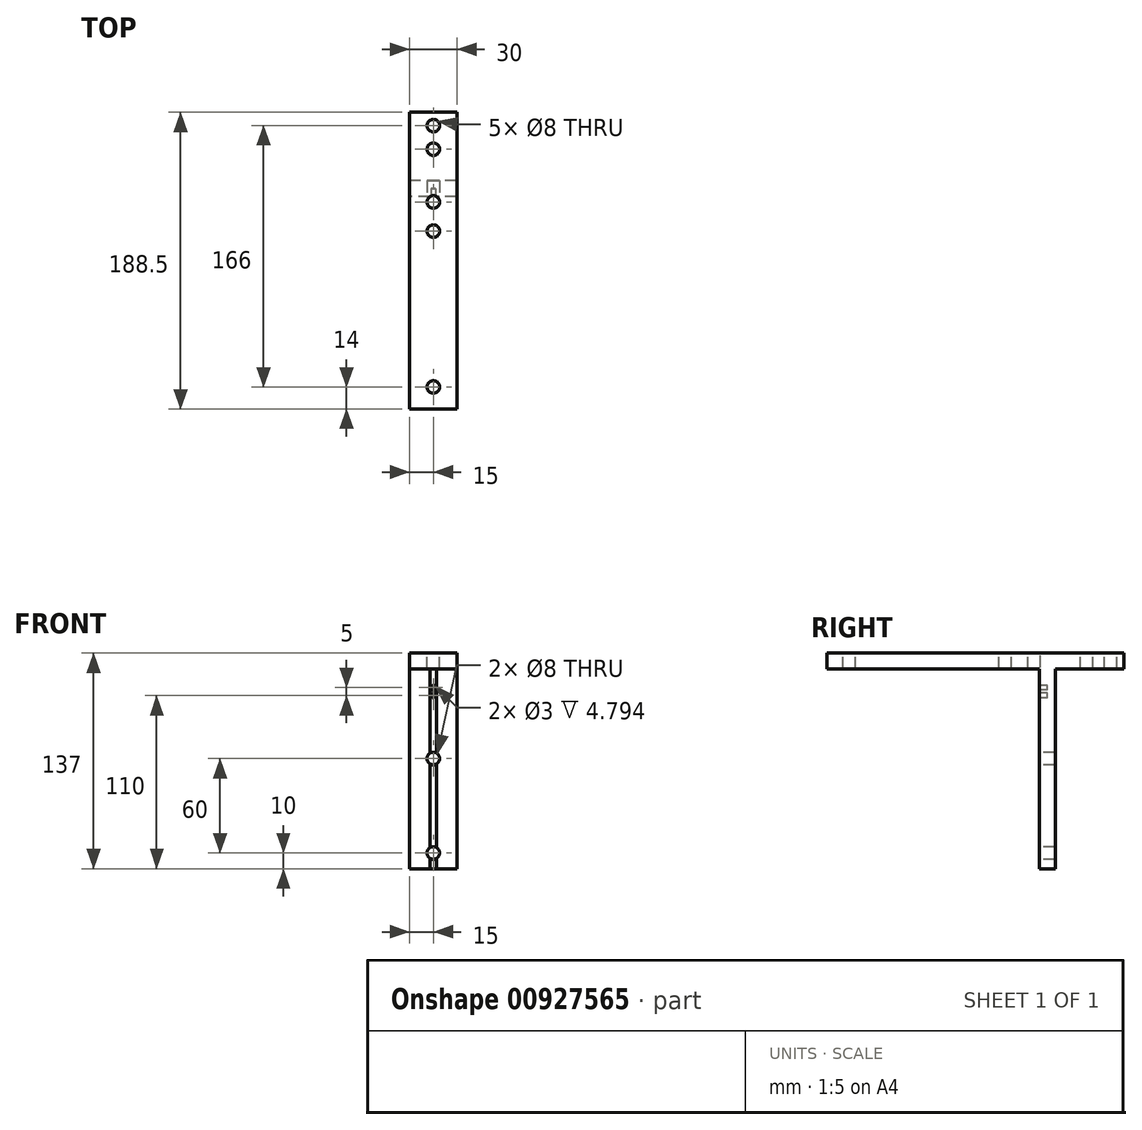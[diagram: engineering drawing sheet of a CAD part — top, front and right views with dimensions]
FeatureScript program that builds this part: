
annotation { "Feature Type Name" : "Feature", "Feature Type Description" : "" }
export const myFeature = defineFeature(function(context is Context, id is Id, definition is map)
    precondition{}
    {
        {
            var Q0;
            Q0=qCreatedBy(makeId("Right.planeOp"),FACE);
            var sketch = newSketch(context, id + "F0", { "sketchPlane" : qUnion([Q0])});
            skLineSegment(sketch, "E0", {"start": v(0, 0) * mm, "end": v(10, 0) * mm});
            skLineSegment(sketch, "E1", {"start": v(10, 0) * mm, "end": v(10, 127) * mm});
            skLineSegment(sketch, "E2", {"start": v(10, 127) * mm, "end": v(53.5, 127) * mm});
            skLineSegment(sketch, "E3", {"start": v(53.5, 127) * mm, "end": v(53.5, 137) * mm});
            skLineSegment(sketch, "E4", {"start": v(53.5, 137) * mm, "end": v(-135, 137) * mm});
            skLineSegment(sketch, "E5", {"start": v(-135, 137) * mm, "end": v(-135, 127) * mm});
            skLineSegment(sketch, "E6", {"start": v(-135, 127) * mm, "end": v(0, 127) * mm});
            skLineSegment(sketch, "E7", {"start": v(0, 127) * mm, "end": v(0, 0) * mm});
            skSolve(sketch);
        }
        {
            var Q0;
            Q0 = qSketchRegion(id + "F0", true);
            extrude(context, id + "F1", {"entities" : qUnion([Q0]), "depth" : 30 * mm, "offsetDistance" : 25 * mm});
        }
        {
            var Q0;
            Q0=makeQuery(id+"F1.opExtrude","SWEPT_FACE",FACE,{"disambiguationData":[OSD([sQuery(id+"F0.wireOp",EDGE,"E7")])]});
            var sketch = newSketch(context, id + "F2", { "sketchPlane" : qUnion([Q0])});
            skLineSegment(sketch, "E8", {"start": v(15, -16.72) * mm, "end": v(15, 133.37) * mm, "construction": true});
            skPoint(sketch, "E8.startSnap0", {"position": v(15, 0) * mm});
            skCircle(sketch, "E9", {"center": v(15, 10) * mm, "radius": 4 * mm});
            skCircle(sketch, "E10", {"center": v(15, 70) * mm, "radius": 4 * mm});
            skSolve(sketch);
        }
        {
            var Q0;
            Q0=makeQuery(id+"F2.imprint","IMPRINT",FACE,{"disambiguationData":[TD([[makeQuery(id+"F2.imprint","IMPRINT",EDGE,{"derivedFrom":sQuery(id+"F2.wireOp",EDGE,"E10")}),1.0]])]});
            var Q1;
            Q1=makeQuery(id+"F2.imprint","IMPRINT",FACE,{"disambiguationData":[TD([[makeQuery(id+"F2.imprint","IMPRINT",EDGE,{"derivedFrom":sQuery(id+"F2.wireOp",EDGE,"E9")}),1.0]])]});
            extrude(context, id + "F3", {"entities" : qUnion([Q0, Q1]), "operationType" : NewBodyOperationType.REMOVE, "endBound" : BoundingType.THROUGH_ALL, "oppositeDirection" : true, "depth" : 25 * mm, "offsetDistance" : 25 * mm});
        }
        {
            var Q0;
            Q0=makeQuery(id+"F1.opExtrude","SWEPT_FACE",FACE,{"disambiguationData":[OSD([sQuery(id+"F0.wireOp",EDGE,"E4")])]});
            var sketch = newSketch(context, id + "F4", { "sketchPlane" : qUnion([Q0])});
            skLineSegment(sketch, "E11", {"start": v(15, 63.57) * mm, "end": v(15, -139.02) * mm, "construction": true});
            skPoint(sketch, "E11.startSnap0", {"position": v(15, 53.5) * mm});
            skPoint(sketch, "E11.endSnap0", {"position": v(15, -135) * mm});
            skCircle(sketch, "E12", {"center": v(15, 45) * mm, "radius": 4 * mm});
            skCircle(sketch, "E13", {"center": v(15, 30) * mm, "radius": 4 * mm});
            skCircle(sketch, "E14", {"center": v(15, -3.5) * mm, "radius": 4 * mm});
            skCircle(sketch, "E15", {"center": v(15, -22) * mm, "radius": 4 * mm});
            skCircle(sketch, "E16", {"center": v(15, -121) * mm, "radius": 4 * mm});
            skSolve(sketch);
        }
        {
            var Q0;
            Q0 = qSketchRegion(id + "F4", true);
            extrude(context, id + "F5", {"entities" : qUnion([Q0]), "operationType" : NewBodyOperationType.REMOVE, "endBound" : BoundingType.THROUGH_ALL, "oppositeDirection" : true, "depth" : 25 * mm, "offsetDistance" : 25 * mm});
        }
        {
            var Q0;
            Q0=makeQuery(id+"F1.opExtrude","SWEPT_FACE",FACE,{"disambiguationData":[OSD([sQuery(id+"F0.wireOp",EDGE,"E7")])]});
            var sketch = newSketch(context, id + "F6", { "sketchPlane" : qUnion([Q0])});
            skCircle(sketch, "E17", {"center": v(15, 110) * mm, "radius": 1.5 * mm});
            skCircle(sketch, "E18", {"center": v(15, 115) * mm, "radius": 1.5 * mm});
            skSolve(sketch);
        }
        {
            var Q0;
            Q0 = qSketchRegion(id + "F6", true);
            extrude(context, id + "F7", {"entities" : qUnion([Q0]), "operationType" : NewBodyOperationType.REMOVE, "oppositeDirection" : true, "depth" : 5 * mm, "offsetDistance" : 25 * mm});
        }
    });
